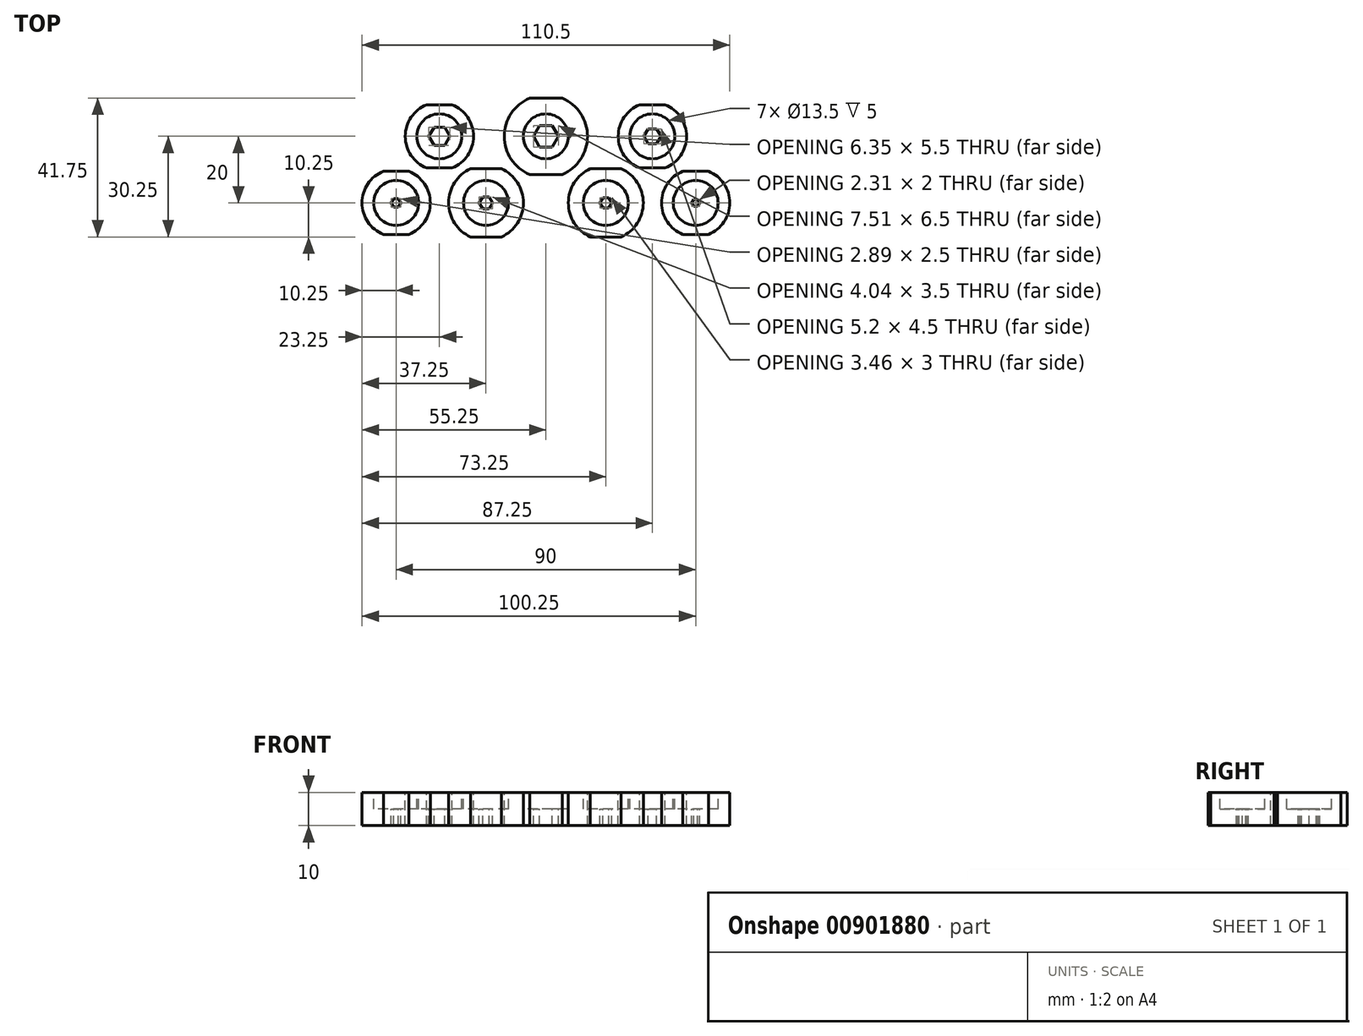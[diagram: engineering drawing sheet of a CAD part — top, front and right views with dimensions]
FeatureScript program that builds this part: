
annotation { "Feature Type Name" : "Feature", "Feature Type Description" : "" }
export const myFeature = defineFeature(function(context is Context, id is Id, definition is map)
    precondition{}
    {
        {
            var Q0;
            Q0=qCreatedBy(makeId("Top.planeOp"),FACE);
            var sketch = newSketch(context, id + "F0", { "sketchPlane" : qUnion([Q0])});
            skLineSegment(sketch, "E0.bottom", {"start": v(-60.5, 25) * mm, "end": v(60.5, 25) * mm});
            skLineSegment(sketch, "E0.top", {"start": v(-60.5, -25) * mm, "end": v(60.5, -25) * mm});
            skLineSegment(sketch, "E0.left", {"start": v(-60.5, 25) * mm, "end": v(-60.5, -25) * mm});
            skLineSegment(sketch, "E0.right", {"start": v(60.5, 25) * mm, "end": v(60.5, -25) * mm});
            skLineSegment(sketch, "E1", {"start": v(-59.03, 10) * mm, "end": v(55.15, 10) * mm, "construction": true});
            skLineSegment(sketch, "E2", {"start": v(-58.22, -10) * mm, "end": v(58.04, -10) * mm, "construction": true});
            skCircle(sketch, "E3", {"center": v(0, 10) * mm, "radius": 6.75 * mm});
            skCircle(sketch, "E4", {"center": v(-18, -10) * mm, "radius": 6.75 * mm});
            skCircle(sketch, "E5", {"center": v(-32, 10) * mm, "radius": 6.75 * mm});
            skCircle(sketch, "E6", {"center": v(-45, -10) * mm, "radius": 6.75 * mm});
            skCircle(sketch, "E7", {"center": v(18, -10) * mm, "radius": 6.75 * mm});
            skCircle(sketch, "E8", {"center": v(32, 10) * mm, "radius": 6.75 * mm});
            skCircle(sketch, "E9", {"center": v(45, -10) * mm, "radius": 6.75 * mm});
            skArc(sketch, "E10", {"start": v(-4.9, 21.5) * mm, "mid": v(-12.5, 10) * mm, "end": v(-4.9, -1.5) * mm});
            skArc(sketch, "E11", {"start": v(-22.64, 0.25) * mm, "mid": v(-29.25, -10) * mm, "end": v(-22.64, -20.25) * mm});
            skArc(sketch, "E12", {"start": v(13.36, 0.25) * mm, "mid": v(6.75, -10) * mm, "end": v(13.36, -20.25) * mm});
            skArc(sketch, "E13", {"start": v(-35.85, 19.5) * mm, "mid": v(-42.25, 10) * mm, "end": v(-35.85, 0.5) * mm});
            skArc(sketch, "E14", {"start": v(-48.85, -0.5) * mm, "mid": v(-55.25, -10) * mm, "end": v(-48.85, -19.5) * mm});
            skArc(sketch, "E15", {"start": v(28.15, 19.5) * mm, "mid": v(21.75, 10) * mm, "end": v(28.15, 0.5) * mm});
            skArc(sketch, "E16", {"start": v(41.15, -0.5) * mm, "mid": v(34.75, -10) * mm, "end": v(41.15, -19.5) * mm});
            skLineSegment(sketch, "E17", {"start": v(-35.85, 19.5) * mm, "end": v(-28.15, 19.5) * mm});
            skLineSegment(sketch, "E18", {"start": v(28.15, 19.5) * mm, "end": v(35.85, 19.5) * mm});
            skLineSegment(sketch, "E19", {"start": v(-48.85, -0.5) * mm, "end": v(-41.15, -0.5) * mm});
            skLineSegment(sketch, "E20", {"start": v(-48.85, -19.5) * mm, "end": v(-41.15, -19.5) * mm});
            skLineSegment(sketch, "E21", {"start": v(-22.64, -20.25) * mm, "end": v(-13.36, -20.25) * mm});
            skLineSegment(sketch, "E22", {"start": v(-22.64, 0.25) * mm, "end": v(-13.36, 0.25) * mm});
            skLineSegment(sketch, "E23", {"start": v(13.36, -20.25) * mm, "end": v(22.64, -20.25) * mm});
            skLineSegment(sketch, "E24", {"start": v(41.15, -19.5) * mm, "end": v(48.85, -19.5) * mm});
            skCircle(sketch, "E25.cCircle", {"center": v(0, 10) * mm, "radius": 3.25 * mm, "construction": true});
            skLineSegment(sketch, "E25.0", {"start": v(1.88, 6.75) * mm, "end": v(-1.88, 6.75) * mm});
            skLineSegment(sketch, "E25.1", {"start": v(-1.88, 6.75) * mm, "end": v(-3.75, 10) * mm});
            skLineSegment(sketch, "E25.2", {"start": v(-3.75, 10) * mm, "end": v(-1.88, 13.25) * mm});
            skLineSegment(sketch, "E25.3", {"start": v(-1.88, 13.25) * mm, "end": v(1.88, 13.25) * mm});
            skLineSegment(sketch, "E25.4", {"start": v(1.88, 13.25) * mm, "end": v(3.75, 10) * mm});
            skLineSegment(sketch, "E25.5", {"start": v(3.75, 10) * mm, "end": v(1.88, 6.75) * mm});
            skPoint(sketch, "E25.0.midPoint", {"position": v(0, 6.75) * mm});
            skCircle(sketch, "E26.cCircle", {"center": v(32, 10) * mm, "radius": 2.25 * mm, "construction": true});
            skLineSegment(sketch, "E26.0", {"start": v(34.6, 10) * mm, "end": v(33.3, 7.75) * mm});
            skLineSegment(sketch, "E26.1", {"start": v(33.3, 7.75) * mm, "end": v(30.7, 7.75) * mm});
            skLineSegment(sketch, "E26.2", {"start": v(30.7, 7.75) * mm, "end": v(29.4, 10) * mm});
            skLineSegment(sketch, "E26.3", {"start": v(29.4, 10) * mm, "end": v(30.7, 12.25) * mm});
            skLineSegment(sketch, "E26.4", {"start": v(30.7, 12.25) * mm, "end": v(33.3, 12.25) * mm});
            skLineSegment(sketch, "E26.5", {"start": v(33.3, 12.25) * mm, "end": v(34.6, 10) * mm});
            skPoint(sketch, "E26.0.midPoint", {"position": v(33.95, 8.88) * mm});
            skCircle(sketch, "E27.cCircle", {"center": v(-32, 10) * mm, "radius": 2.75 * mm, "construction": true});
            skLineSegment(sketch, "E27.0", {"start": v(-30.41, 12.75) * mm, "end": v(-28.82, 10) * mm});
            skLineSegment(sketch, "E27.1", {"start": v(-28.82, 10) * mm, "end": v(-30.41, 7.25) * mm});
            skLineSegment(sketch, "E27.2", {"start": v(-30.41, 7.25) * mm, "end": v(-33.59, 7.25) * mm});
            skLineSegment(sketch, "E27.3", {"start": v(-33.59, 7.25) * mm, "end": v(-35.18, 10) * mm});
            skLineSegment(sketch, "E27.4", {"start": v(-35.18, 10) * mm, "end": v(-33.59, 12.75) * mm});
            skLineSegment(sketch, "E27.5", {"start": v(-33.59, 12.75) * mm, "end": v(-30.41, 12.75) * mm});
            skPoint(sketch, "E27.0.midPoint", {"position": v(-29.62, 11.38) * mm});
            skCircle(sketch, "E28.cCircle", {"center": v(-45, -10) * mm, "radius": 1.25 * mm, "construction": true});
            skLineSegment(sketch, "E28.0", {"start": v(-43.56, -10) * mm, "end": v(-44.28, -11.25) * mm});
            skLineSegment(sketch, "E28.1", {"start": v(-44.28, -11.25) * mm, "end": v(-45.72, -11.25) * mm});
            skLineSegment(sketch, "E28.2", {"start": v(-45.72, -11.25) * mm, "end": v(-46.44, -10) * mm});
            skLineSegment(sketch, "E28.3", {"start": v(-46.44, -10) * mm, "end": v(-45.72, -8.75) * mm});
            skLineSegment(sketch, "E28.4", {"start": v(-45.72, -8.75) * mm, "end": v(-44.28, -8.75) * mm});
            skLineSegment(sketch, "E28.5", {"start": v(-44.28, -8.75) * mm, "end": v(-43.56, -10) * mm});
            skPoint(sketch, "E28.0.midPoint", {"position": v(-43.92, -10.63) * mm});
            skCircle(sketch, "E29.cCircle", {"center": v(-18, -10) * mm, "radius": 1.75 * mm, "construction": true});
            skLineSegment(sketch, "E29.0", {"start": v(-16.99, -11.75) * mm, "end": v(-19.01, -11.75) * mm});
            skLineSegment(sketch, "E29.1", {"start": v(-19.01, -11.75) * mm, "end": v(-20.02, -10) * mm});
            skLineSegment(sketch, "E29.2", {"start": v(-20.02, -10) * mm, "end": v(-19.01, -8.25) * mm});
            skLineSegment(sketch, "E29.3", {"start": v(-19.01, -8.25) * mm, "end": v(-16.99, -8.25) * mm});
            skLineSegment(sketch, "E29.4", {"start": v(-16.99, -8.25) * mm, "end": v(-15.98, -10) * mm});
            skLineSegment(sketch, "E29.5", {"start": v(-15.98, -10) * mm, "end": v(-16.99, -11.75) * mm});
            skPoint(sketch, "E29.0.midPoint", {"position": v(-18, -11.75) * mm});
            skCircle(sketch, "E30.cCircle", {"center": v(18, -10) * mm, "radius": 1.5 * mm, "construction": true});
            skLineSegment(sketch, "E30.0", {"start": v(18.87, -11.5) * mm, "end": v(17.13, -11.5) * mm});
            skLineSegment(sketch, "E30.1", {"start": v(17.13, -11.5) * mm, "end": v(16.27, -10) * mm});
            skLineSegment(sketch, "E30.2", {"start": v(16.27, -10) * mm, "end": v(17.13, -8.5) * mm});
            skLineSegment(sketch, "E30.3", {"start": v(17.13, -8.5) * mm, "end": v(18.87, -8.5) * mm});
            skLineSegment(sketch, "E30.4", {"start": v(18.87, -8.5) * mm, "end": v(19.73, -10) * mm});
            skLineSegment(sketch, "E30.5", {"start": v(19.73, -10) * mm, "end": v(18.87, -11.5) * mm});
            skPoint(sketch, "E30.0.midPoint", {"position": v(18, -11.5) * mm});
            skCircle(sketch, "E31.cCircle", {"center": v(45, -10) * mm, "radius": 1 * mm, "construction": true});
            skLineSegment(sketch, "E31.0", {"start": v(45.58, -11) * mm, "end": v(44.42, -11) * mm});
            skLineSegment(sketch, "E31.1", {"start": v(44.42, -11) * mm, "end": v(43.85, -10) * mm});
            skLineSegment(sketch, "E31.2", {"start": v(43.85, -10) * mm, "end": v(44.42, -9) * mm});
            skLineSegment(sketch, "E31.3", {"start": v(44.42, -9) * mm, "end": v(45.58, -9) * mm});
            skLineSegment(sketch, "E31.4", {"start": v(45.58, -9) * mm, "end": v(46.15, -10) * mm});
            skLineSegment(sketch, "E31.5", {"start": v(46.15, -10) * mm, "end": v(45.58, -11) * mm});
            skPoint(sketch, "E31.0.midPoint", {"position": v(45, -11) * mm});
            skLineSegment(sketch, "E32", {"start": v(-4.9, 21.5) * mm, "end": v(4.9, 21.5) * mm});
            skLineSegment(sketch, "E33", {"start": v(-35.85, 0.5) * mm, "end": v(-28.15, 0.5) * mm});
            skArc(sketch, "E34.trimOffspring", {"start": v(-28.15, 0.5) * mm, "mid": v(-21.75, 10) * mm, "end": v(-28.15, 19.5) * mm});
            skLineSegment(sketch, "E35", {"start": v(28.15, 0.5) * mm, "end": v(35.85, 0.5) * mm});
            skArc(sketch, "E36.trimOffspring", {"start": v(35.85, 0.5) * mm, "mid": v(42.25, 10) * mm, "end": v(35.85, 19.5) * mm});
            skLineSegment(sketch, "E37", {"start": v(-4.9, -1.5) * mm, "end": v(4.9, -1.5) * mm});
            skArc(sketch, "E38.trimOffspring", {"start": v(4.9, -1.5) * mm, "mid": v(12.5, 10) * mm, "end": v(4.9, 21.5) * mm});
            skLineSegment(sketch, "E39", {"start": v(41.15, -0.5) * mm, "end": v(48.85, -0.5) * mm});
            skArc(sketch, "E40.trimOffspring", {"start": v(-41.15, -19.5) * mm, "mid": v(-34.75, -10) * mm, "end": v(-41.15, -0.5) * mm});
            skArc(sketch, "E41.trimOffspring", {"start": v(-13.36, -20.25) * mm, "mid": v(-6.75, -10) * mm, "end": v(-13.36, 0.25) * mm});
            skLineSegment(sketch, "E42.trimOffspring", {"start": v(13.36, 0.25) * mm, "end": v(22.64, 0.25) * mm});
            skArc(sketch, "E43.trimOffspring", {"start": v(22.64, -20.25) * mm, "mid": v(29.25, -10) * mm, "end": v(22.64, 0.25) * mm});
            skArc(sketch, "E44.trimOffspring", {"start": v(48.85, -19.5) * mm, "mid": v(55.25, -10) * mm, "end": v(48.85, -0.5) * mm});
            skLineSegment(sketch, "E45", {"start": v(-37.07, 28.29) * mm, "end": v(-60.5, -7.69) * mm});
            skLineSegment(sketch, "E46", {"start": v(-40.92, 15.05) * mm, "end": v(-44.27, 17.23) * mm});
            skLineSegment(sketch, "E47", {"start": v(37.1, 28.29) * mm, "end": v(60.5, -7.7) * mm});
            skLineSegment(sketch, "E48", {"start": v(-47.03, -28.17) * mm, "end": v(47.18, -28.17) * mm});
            skLineSegment(sketch, "E49", {"start": v(47.18, -28.17) * mm, "end": v(60.5, -14.79) * mm});
            skLineSegment(sketch, "E50", {"start": v(-37.07, 28.29) * mm, "end": v(-67.24, 28.29) * mm});
            skLineSegment(sketch, "E51", {"start": v(-67.24, 28.29) * mm, "end": v(-67.24, -28.17) * mm});
            skLineSegment(sketch, "E52", {"start": v(-67.24, -28.17) * mm, "end": v(-47.03, -34.83) * mm});
            skLineSegment(sketch, "E53", {"start": v(-47.03, -34.83) * mm, "end": v(47.18, -34.83) * mm});
            skLineSegment(sketch, "E54", {"start": v(47.18, -34.83) * mm, "end": v(67.7, -26.04) * mm});
            skLineSegment(sketch, "E55", {"start": v(67.7, -26.04) * mm, "end": v(67.7, 28.29) * mm});
            skLineSegment(sketch, "E56", {"start": v(67.7, 28.29) * mm, "end": v(37.1, 28.29) * mm});
            skPoint(sketch, "E57.trimOffspring.end.orphan", {"position": v(65.27, -10) * mm});
            skPoint(sketch, "E58.trimOffspring.end.orphan", {"position": v(64.43, -13.75) * mm});
            skLineSegment(sketch, "E59.trimOffspring", {"start": v(-60.5, -12.88) * mm, "end": v(-47.03, -28.17) * mm});
            skPoint(sketch, "E60.start.orphan", {"position": v(-64.45, -8.4) * mm});
            skPoint(sketch, "E61.trimOffspring.end.orphan", {"position": v(-64.45, -13.75) * mm});
            skSolve(sketch);
        }
        {
            var Q0;
            Q0=makeQuery(id+"F0.imprint","IMPRINT",FACE,{"disambiguationData":[TD([[makeQuery(id+"F0.imprint","IMPRINT",EDGE,{"derivedFrom":sQuery(id+"F0.wireOp",EDGE,"E6")}),-1.0]])]});
            var Q1;
            Q1=makeQuery(id+"F0.imprint","IMPRINT",FACE,{"disambiguationData":[TD([[makeQuery(id+"F0.imprint","IMPRINT",EDGE,{"derivedFrom":sQuery(id+"F0.wireOp",EDGE,"E6")}),1.0]])]});
            var Q2;
            Q2=makeQuery(id+"F0.imprint","IMPRINT",FACE,{"disambiguationData":[TD([[makeQuery(id+"F0.imprint","IMPRINT",EDGE,{"derivedFrom":sQuery(id+"F0.wireOp",EDGE,"E28.0")}),-1.0]])]});
            var Q3;
            Q3=makeQuery(id+"F0.imprint","IMPRINT",FACE,{"disambiguationData":[TD([[makeQuery(id+"F0.imprint","IMPRINT",EDGE,{"derivedFrom":sQuery(id+"F0.wireOp",EDGE,"E5")}),-1.0]])]});
            var Q4;
            Q4=makeQuery(id+"F0.imprint","IMPRINT",FACE,{"disambiguationData":[TD([[makeQuery(id+"F0.imprint","IMPRINT",EDGE,{"derivedFrom":sQuery(id+"F0.wireOp",EDGE,"E5")}),1.0]])]});
            var Q5;
            Q5=makeQuery(id+"F0.imprint","IMPRINT",FACE,{"disambiguationData":[TD([[makeQuery(id+"F0.imprint","IMPRINT",EDGE,{"derivedFrom":sQuery(id+"F0.wireOp",EDGE,"E27.0")}),-1.0]])]});
            var Q6;
            Q6=makeQuery(id+"F0.imprint","IMPRINT",FACE,{"disambiguationData":[TD([[makeQuery(id+"F0.imprint","IMPRINT",EDGE,{"derivedFrom":sQuery(id+"F0.wireOp",EDGE,"E29.0")}),-1.0]])]});
            var Q7;
            Q7=makeQuery(id+"F0.imprint","IMPRINT",FACE,{"disambiguationData":[TD([[makeQuery(id+"F0.imprint","IMPRINT",EDGE,{"derivedFrom":sQuery(id+"F0.wireOp",EDGE,"E4")}),1.0]])]});
            var Q8;
            Q8=makeQuery(id+"F0.imprint","IMPRINT",FACE,{"disambiguationData":[TD([[makeQuery(id+"F0.imprint","IMPRINT",EDGE,{"derivedFrom":sQuery(id+"F0.wireOp",EDGE,"E4")}),-1.0]])]});
            var Q9;
            Q9=makeQuery(id+"F0.imprint","IMPRINT",FACE,{"disambiguationData":[TD([[makeQuery(id+"F0.imprint","IMPRINT",EDGE,{"derivedFrom":sQuery(id+"F0.wireOp",EDGE,"E25.0")}),-1.0]])]});
            var Q10;
            Q10=makeQuery(id+"F0.imprint","IMPRINT",FACE,{"disambiguationData":[TD([[makeQuery(id+"F0.imprint","IMPRINT",EDGE,{"derivedFrom":sQuery(id+"F0.wireOp",EDGE,"E3")}),1.0]])]});
            var Q11;
            Q11=makeQuery(id+"F0.imprint","IMPRINT",FACE,{"disambiguationData":[TD([[makeQuery(id+"F0.imprint","IMPRINT",EDGE,{"derivedFrom":sQuery(id+"F0.wireOp",EDGE,"E3")}),-1.0]])]});
            var Q12;
            Q12=makeQuery(id+"F0.imprint","IMPRINT",FACE,{"disambiguationData":[TD([[makeQuery(id+"F0.imprint","IMPRINT",EDGE,{"derivedFrom":sQuery(id+"F0.wireOp",EDGE,"E30.0")}),-1.0]])]});
            var Q13;
            Q13=makeQuery(id+"F0.imprint","IMPRINT",FACE,{"disambiguationData":[TD([[makeQuery(id+"F0.imprint","IMPRINT",EDGE,{"derivedFrom":sQuery(id+"F0.wireOp",EDGE,"E7")}),1.0]])]});
            var Q14;
            Q14=makeQuery(id+"F0.imprint","IMPRINT",FACE,{"disambiguationData":[TD([[makeQuery(id+"F0.imprint","IMPRINT",EDGE,{"derivedFrom":sQuery(id+"F0.wireOp",EDGE,"E7")}),-1.0]])]});
            var Q15;
            Q15=makeQuery(id+"F0.imprint","IMPRINT",FACE,{"disambiguationData":[TD([[makeQuery(id+"F0.imprint","IMPRINT",EDGE,{"derivedFrom":sQuery(id+"F0.wireOp",EDGE,"E26.0")}),-1.0]])]});
            var Q16;
            Q16=makeQuery(id+"F0.imprint","IMPRINT",FACE,{"disambiguationData":[TD([[makeQuery(id+"F0.imprint","IMPRINT",EDGE,{"derivedFrom":sQuery(id+"F0.wireOp",EDGE,"E8")}),1.0]])]});
            var Q17;
            Q17=makeQuery(id+"F0.imprint","IMPRINT",FACE,{"disambiguationData":[TD([[makeQuery(id+"F0.imprint","IMPRINT",EDGE,{"derivedFrom":sQuery(id+"F0.wireOp",EDGE,"E8")}),-1.0]])]});
            var Q18;
            Q18=makeQuery(id+"F0.imprint","IMPRINT",FACE,{"disambiguationData":[TD([[makeQuery(id+"F0.imprint","IMPRINT",EDGE,{"derivedFrom":sQuery(id+"F0.wireOp",EDGE,"E31.0")}),-1.0]])]});
            var Q19;
            Q19=makeQuery(id+"F0.imprint","IMPRINT",FACE,{"disambiguationData":[TD([[makeQuery(id+"F0.imprint","IMPRINT",EDGE,{"derivedFrom":sQuery(id+"F0.wireOp",EDGE,"E9")}),1.0]])]});
            var Q20;
            Q20=makeQuery(id+"F0.imprint","IMPRINT",FACE,{"disambiguationData":[TD([[makeQuery(id+"F0.imprint","IMPRINT",EDGE,{"derivedFrom":sQuery(id+"F0.wireOp",EDGE,"E9")}),-1.0]])]});
            var Q21;
            Q21=makeQuery(id+"F0.imprint","IMPRINT",FACE,{"disambiguationData":[TD([[makeQuery(id+"F0.imprint","IMPRINT",EDGE,{"derivedFrom":sQuery(id+"F0.wireOp",EDGE,"E10")}),-1.0]])]});
            extrude(context, id + "F1", {"entities" : qUnion([Q0, Q1, Q2, Q3, Q4, Q5, Q6, Q7, Q8, Q9, Q10, Q11, Q12, Q13, Q14, Q15, Q16, Q17, Q18, Q19, Q20, Q21]), "oppositeDirection" : true, "depth" : 20 * mm, "offsetDistance" : 25 * mm});
        }
        {
            var Q0;
            Q0=makeQuery(id+"F0.imprint","IMPRINT",FACE,{"disambiguationData":[TD([[makeQuery(id+"F0.imprint","IMPRINT",EDGE,{"derivedFrom":sQuery(id+"F0.wireOp",EDGE,"E27.0")}),-1.0]])]});
            var Q1;
            Q1=makeQuery(id+"F0.imprint","IMPRINT",FACE,{"disambiguationData":[TD([[makeQuery(id+"F0.imprint","IMPRINT",EDGE,{"derivedFrom":sQuery(id+"F0.wireOp",EDGE,"E25.0")}),-1.0]])]});
            var Q2;
            Q2=makeQuery(id+"F0.imprint","IMPRINT",FACE,{"disambiguationData":[TD([[makeQuery(id+"F0.imprint","IMPRINT",EDGE,{"derivedFrom":sQuery(id+"F0.wireOp",EDGE,"E26.0")}),-1.0]])]});
            var Q3;
            Q3=makeQuery(id+"F0.imprint","IMPRINT",FACE,{"disambiguationData":[TD([[makeQuery(id+"F0.imprint","IMPRINT",EDGE,{"derivedFrom":sQuery(id+"F0.wireOp",EDGE,"E28.0")}),-1.0]])]});
            var Q4;
            Q4=makeQuery(id+"F0.imprint","IMPRINT",FACE,{"disambiguationData":[TD([[makeQuery(id+"F0.imprint","IMPRINT",EDGE,{"derivedFrom":sQuery(id+"F0.wireOp",EDGE,"E29.0")}),-1.0]])]});
            var Q5;
            Q5=makeQuery(id+"F0.imprint","IMPRINT",FACE,{"disambiguationData":[TD([[makeQuery(id+"F0.imprint","IMPRINT",EDGE,{"derivedFrom":sQuery(id+"F0.wireOp",EDGE,"E30.0")}),-1.0]])]});
            var Q6;
            Q6=makeQuery(id+"F0.imprint","IMPRINT",FACE,{"disambiguationData":[TD([[makeQuery(id+"F0.imprint","IMPRINT",EDGE,{"derivedFrom":sQuery(id+"F0.wireOp",EDGE,"E31.0")}),-1.0]])]});
            extrude(context, id + "F2", {"entities" : qUnion([Q0, Q1, Q2, Q3, Q4, Q5, Q6]), "operationType" : NewBodyOperationType.REMOVE, "oppositeDirection" : true, "depth" : 25 * mm, "offsetDistance" : 25 * mm});
        }
        {
            var Q0;
            Q0=makeQuery(id+"F0.imprint","IMPRINT",FACE,{"disambiguationData":[TD([[makeQuery(id+"F0.imprint","IMPRINT",EDGE,{"derivedFrom":sQuery(id+"F0.wireOp",EDGE,"E5")}),1.0]])]});
            var Q1;
            Q1=makeQuery(id+"F0.imprint","IMPRINT",FACE,{"disambiguationData":[TD([[makeQuery(id+"F0.imprint","IMPRINT",EDGE,{"derivedFrom":sQuery(id+"F0.wireOp",EDGE,"E3")}),1.0]])]});
            var Q2;
            Q2=makeQuery(id+"F0.imprint","IMPRINT",FACE,{"disambiguationData":[TD([[makeQuery(id+"F0.imprint","IMPRINT",EDGE,{"derivedFrom":sQuery(id+"F0.wireOp",EDGE,"E8")}),1.0]])]});
            var Q3;
            Q3=makeQuery(id+"F0.imprint","IMPRINT",FACE,{"disambiguationData":[TD([[makeQuery(id+"F0.imprint","IMPRINT",EDGE,{"derivedFrom":sQuery(id+"F0.wireOp",EDGE,"E9")}),1.0]])]});
            var Q4;
            Q4=makeQuery(id+"F0.imprint","IMPRINT",FACE,{"disambiguationData":[TD([[makeQuery(id+"F0.imprint","IMPRINT",EDGE,{"derivedFrom":sQuery(id+"F0.wireOp",EDGE,"E7")}),1.0]])]});
            var Q5;
            Q5=makeQuery(id+"F0.imprint","IMPRINT",FACE,{"disambiguationData":[TD([[makeQuery(id+"F0.imprint","IMPRINT",EDGE,{"derivedFrom":sQuery(id+"F0.wireOp",EDGE,"E4")}),1.0]])]});
            var Q6;
            Q6=makeQuery(id+"F0.imprint","IMPRINT",FACE,{"disambiguationData":[TD([[makeQuery(id+"F0.imprint","IMPRINT",EDGE,{"derivedFrom":sQuery(id+"F0.wireOp",EDGE,"E6")}),1.0]])]});
            extrude(context, id + "F3", {"entities" : qUnion([Q0, Q1, Q2, Q3, Q4, Q5, Q6]), "operationType" : NewBodyOperationType.REMOVE, "oppositeDirection" : true, "depth" : 15 * mm, "offsetDistance" : 25 * mm});
        }
        {
            var Q0;
            Q0=makeQuery(id+"F0.imprint","IMPRINT",FACE,{"disambiguationData":[TD([[makeQuery(id+"F0.imprint","IMPRINT",EDGE,{"derivedFrom":sQuery(id+"F0.wireOp",EDGE,"E6")}),-1.0]])]});
            var Q1;
            Q1=makeQuery(id+"F0.imprint","IMPRINT",FACE,{"disambiguationData":[TD([[makeQuery(id+"F0.imprint","IMPRINT",EDGE,{"derivedFrom":sQuery(id+"F0.wireOp",EDGE,"E5")}),-1.0]])]});
            var Q2;
            Q2=makeQuery(id+"F0.imprint","IMPRINT",FACE,{"disambiguationData":[TD([[makeQuery(id+"F0.imprint","IMPRINT",EDGE,{"derivedFrom":sQuery(id+"F0.wireOp",EDGE,"E3")}),-1.0]])]});
            var Q3;
            Q3=makeQuery(id+"F0.imprint","IMPRINT",FACE,{"disambiguationData":[TD([[makeQuery(id+"F0.imprint","IMPRINT",EDGE,{"derivedFrom":sQuery(id+"F0.wireOp",EDGE,"E8")}),-1.0]])]});
            var Q4;
            Q4=makeQuery(id+"F0.imprint","IMPRINT",FACE,{"disambiguationData":[TD([[makeQuery(id+"F0.imprint","IMPRINT",EDGE,{"derivedFrom":sQuery(id+"F0.wireOp",EDGE,"E9")}),-1.0]])]});
            var Q5;
            Q5=makeQuery(id+"F0.imprint","IMPRINT",FACE,{"disambiguationData":[TD([[makeQuery(id+"F0.imprint","IMPRINT",EDGE,{"derivedFrom":sQuery(id+"F0.wireOp",EDGE,"E7")}),-1.0]])]});
            var Q6;
            Q6=makeQuery(id+"F0.imprint","IMPRINT",FACE,{"disambiguationData":[TD([[makeQuery(id+"F0.imprint","IMPRINT",EDGE,{"derivedFrom":sQuery(id+"F0.wireOp",EDGE,"E4")}),-1.0]])]});
            extrude(context, id + "F4", {"entities" : qUnion([Q0, Q1, Q2, Q3, Q4, Q5, Q6]), "operationType" : NewBodyOperationType.REMOVE, "oppositeDirection" : true, "depth" : 10 * mm, "offsetDistance" : 25 * mm});
        }
        {
            var Q0;
            Q0=qCreatedBy(makeId("Front.planeOp"),FACE);
            cPlane(context, id + "F5", {"entities" : qUnion([Q0]), "cplaneType" : CPlaneType.OFFSET, "offset" : 29 * mm, "oppositeDirection" : true, "width" : 150 * mm, "height" : 150 * mm});
        }
    });
